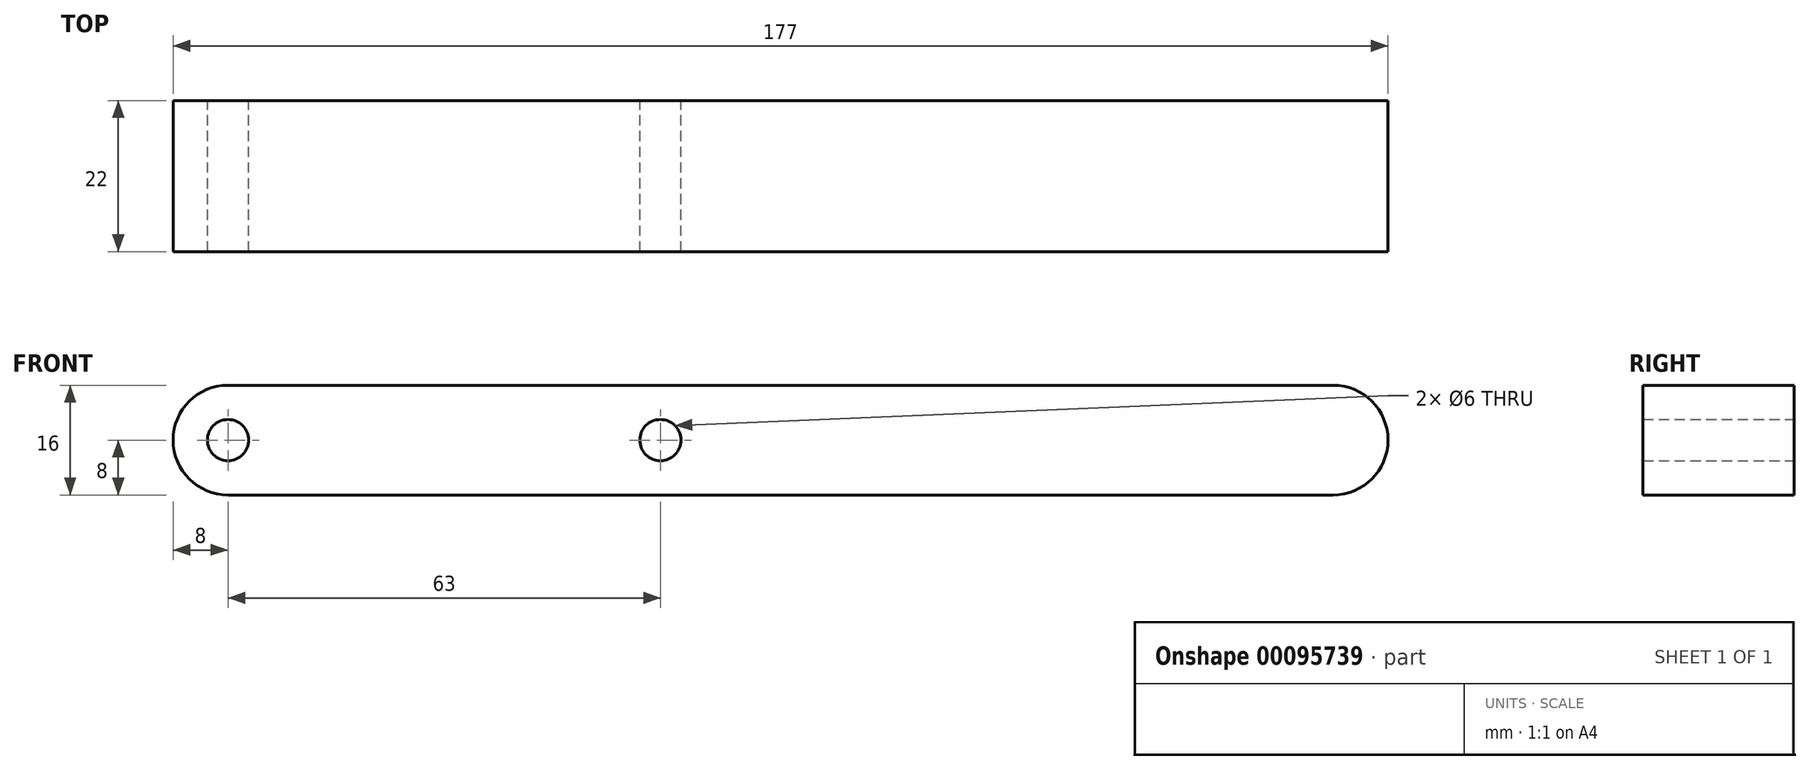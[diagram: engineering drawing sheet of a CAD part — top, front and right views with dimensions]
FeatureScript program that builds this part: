
annotation { "Feature Type Name" : "Feature", "Feature Type Description" : "" }
export const myFeature = defineFeature(function(context is Context, id is Id, definition is map)
    precondition{}
    {
        {
            var Q0;
            Q0=qCreatedBy(makeId("Front.planeOp"),FACE);
            var sketch = newSketch(context, id + "F0", { "sketchPlane" : qUnion([Q0])});
            skCircle(sketch, "E0", {"center": v(0, 0) * mm, "radius": 8 * mm});
            skLineSegment(sketch, "E1", {"start": v(0, 8) * mm, "end": v(-72, 8) * mm});
            skLineSegment(sketch, "E2", {"start": v(0, -8) * mm, "end": v(-72, -8) * mm});
            skLineSegment(sketch, "E3", {"start": v(0, 8) * mm, "end": v(0, -8) * mm});
            skLineSegment(sketch, "E4", {"start": v(-72, 8) * mm, "end": v(-72, -8) * mm});
            skLineSegment(sketch, "E5", {"start": v(-72, -8) * mm, "end": v(-80, -8) * mm});
            skLineSegment(sketch, "E6", {"start": v(-72, 8) * mm, "end": v(-80, 8) * mm});
            skLineSegment(sketch, "E7", {"start": v(-80, 8) * mm, "end": v(-80, -8) * mm});
            skLineSegment(sketch, "E8", {"start": v(-80, 8) * mm, "end": v(-104, 8) * mm});
            skLineSegment(sketch, "E9", {"start": v(-80, -8) * mm, "end": v(-104, -8) * mm});
            skLineSegment(sketch, "E10", {"start": v(-104, 8) * mm, "end": v(-104, -8) * mm});
            skLineSegment(sketch, "E11", {"start": v(-104, 0) * mm, "end": v(-98, 0) * mm, "construction": true});
            skCircle(sketch, "E12", {"center": v(-98, 0) * mm, "radius": 3 * mm});
            skLineSegment(sketch, "E13", {"start": v(-104, 8) * mm, "end": v(-112, 8) * mm});
            skLineSegment(sketch, "E14", {"start": v(-104, -8) * mm, "end": v(-112, -8) * mm});
            skLineSegment(sketch, "E15", {"start": v(-112, 8) * mm, "end": v(-112, -8) * mm});
            skLineSegment(sketch, "E16", {"start": v(-112, 8) * mm, "end": v(-147, 8) * mm});
            skLineSegment(sketch, "E17", {"start": v(-112, -8) * mm, "end": v(-147, -8) * mm});
            skLineSegment(sketch, "E18", {"start": v(-147, 8) * mm, "end": v(-147, -8) * mm});
            skLineSegment(sketch, "E19", {"start": v(-147, 8) * mm, "end": v(-155, 8) * mm});
            skLineSegment(sketch, "E20", {"start": v(-147, -8) * mm, "end": v(-155, -8) * mm});
            skLineSegment(sketch, "E21", {"start": v(-155, 8) * mm, "end": v(-155, -8) * mm});
            skLineSegment(sketch, "E22", {"start": v(-155, 8) * mm, "end": v(-161, 8) * mm});
            skLineSegment(sketch, "E23", {"start": v(-155, -8) * mm, "end": v(-161, -8) * mm});
            skLineSegment(sketch, "E24", {"start": v(-161, 8) * mm, "end": v(-161, -8) * mm, "construction": true});
            skCircle(sketch, "E25", {"center": v(-161, 0) * mm, "radius": 3 * mm});
            skArc(sketch, "E26", {"start": v(-161, 8) * mm, "mid": v(-169, 0) * mm, "end": v(-161, -8) * mm});
            skSolve(sketch);
        }
        {
            var Q0;
            Q0 = qSketchRegion(id + "F0", true);
            extrude(context, id + "F1", {"entities" : qUnion([Q0]), "depth" : 6 * mm});
        }
        {
            var Q0;
            Q0 = qSketchRegion(id + "F0", true);
            extrude(context, id + "F2", {"entities" : qUnion([Q0]), "operationType" : NewBodyOperationType.ADD, "depth" : 22 * mm});
        }
    });
